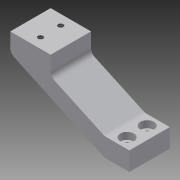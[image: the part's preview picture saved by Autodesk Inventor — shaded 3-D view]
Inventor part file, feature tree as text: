
AUTODESK INVENTOR PART (.ipt)
format: ipt  version: 2014 (Build 180170000, 170)  size: 143,872 bytes
history: native  units: in
note: dims shown in document units (in); Inventor stores cm internally (conversion verified against a paired STEP export)
features: fillet x4, sketch x3, hole x2, extrude x1
ambient origin geometry x8: Origin, YZ Plane, XZ Plane, XY Plane, X Axis, Y Axis, Z Axis, Center Point
bodies: Solid2 (feature_tree)
feature tree (10):
  extrude  "Extrusion2"  Depth=0.65in
  hole  "Hole5"  [1 undecoded]
  hole  "Hole6"  [1 undecoded]
  fillet  "Fillet5"  Radius=0.7874in
  fillet  "Fillet6"  Radius=0.7874in
  fillet  "Fillet7"  Radius=0.7874in
  fillet  "Fillet8"  Radius=0.7874in
  sketch  "Sketch1"  dims[d3=0.3in d4=0.65in]
  sketch  "Sketch7"  dims[d39=1.0in d46=0.25in]
  sketch  "Sketch8"  dims[d74=0.65in d75=0.0in d76=0.7874in d78=0.1625in d79=0.7874in d81=0.1625in d84=0.085in d85=0.75in d86=0.375in d87=0.25in d88=0.5635in d89=1.0in d90=0.8108in d91=0.7874in d93=0.1625in d94=0.7874in d96=0.1625in d99=0.129in d100=0.75in d101=0.219in d102=0.112in d103=0.5635in d104=1.0in d105=0.8108in d106=0.125in d107=0.125in d108=0.125in d109=0.125in d38=1.0in]
note: 2 required parameter values undecoded (feature->parameter linkage not recoverable at this tier; creation-order binding heuristic only, values carry confidence <= 0.55)
